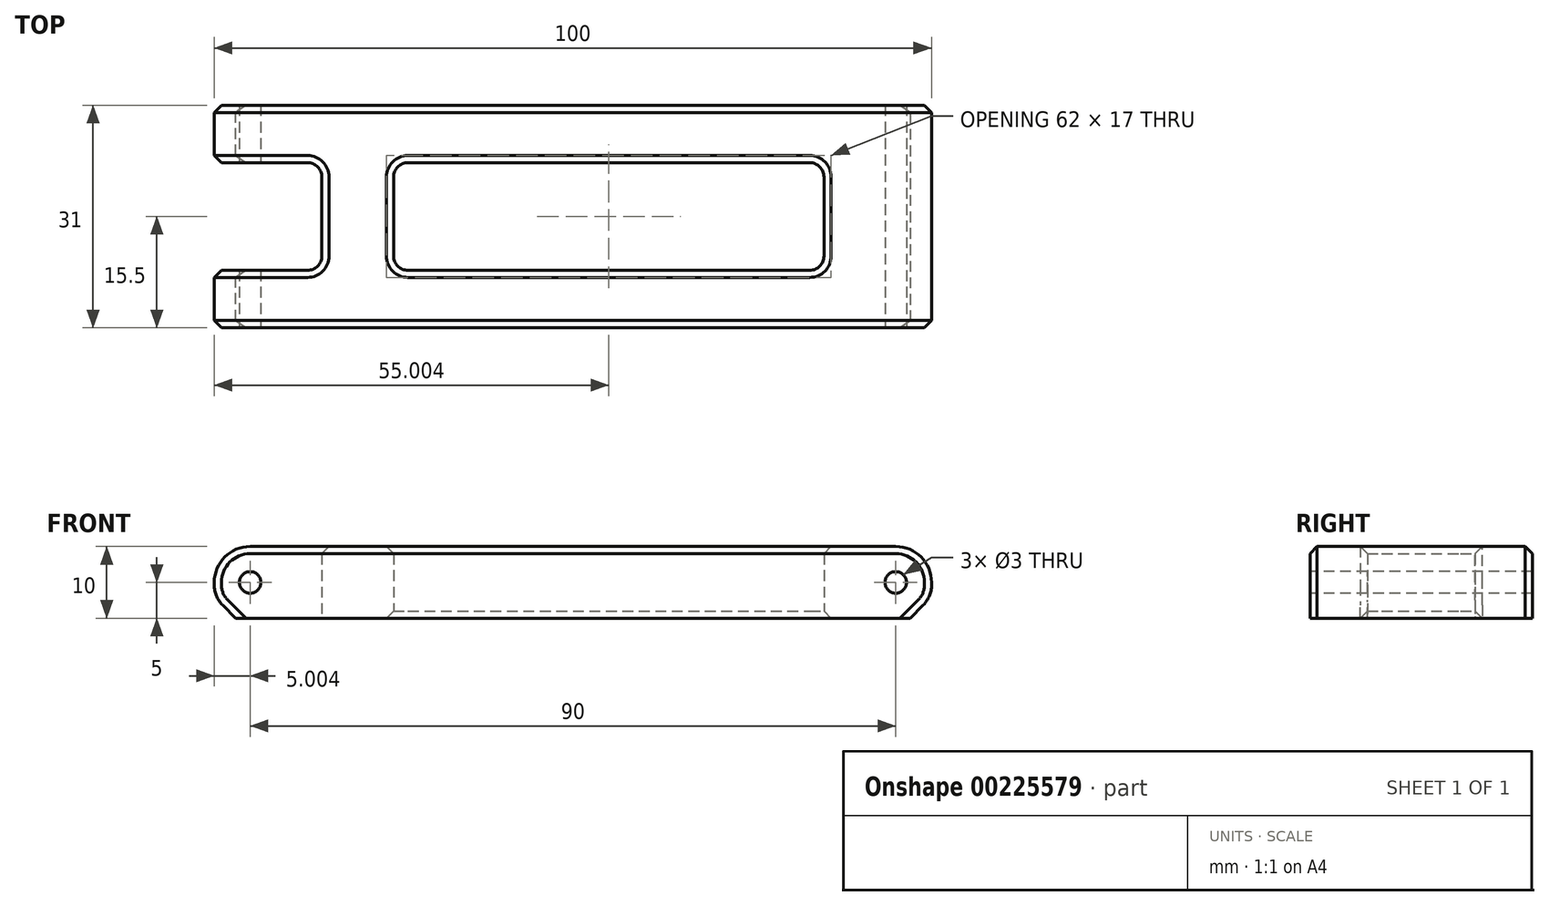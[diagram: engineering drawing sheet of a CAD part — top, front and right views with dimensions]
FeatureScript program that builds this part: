
annotation { "Feature Type Name" : "Feature", "Feature Type Description" : "" }
export const myFeature = defineFeature(function(context is Context, id is Id, definition is map)
    precondition{}
    {
        {
            var Q0;
            Q0=qCreatedBy(makeId("Top.planeOp"),FACE);
            var sketch = newSketch(context, id + "F0", { "sketchPlane" : qUnion([Q0])});
            skLineSegment(sketch, "E0", {"start": v(-23.95, 7.5) * mm, "end": v(-8.95, 7.5) * mm});
            skLineSegment(sketch, "E1", {"start": v(-8.95, 7.5) * mm, "end": v(-8.95, -7.5) * mm});
            skLineSegment(sketch, "E2", {"start": v(-8.95, -7.5) * mm, "end": v(-23.95, -7.5) * mm});
            skLineSegment(sketch, "E3", {"start": v(-23.95, -7.5) * mm, "end": v(-23.95, -15.5) * mm});
            skLineSegment(sketch, "E4", {"start": v(-23.95, -15.5) * mm, "end": v(76.05, -15.5) * mm});
            skLineSegment(sketch, "E5", {"start": v(76.05, -15.5) * mm, "end": v(76.05, 15.5) * mm});
            skLineSegment(sketch, "E6", {"start": v(76.05, 15.5) * mm, "end": v(-23.95, 15.5) * mm});
            skLineSegment(sketch, "E7", {"start": v(-23.95, 15.5) * mm, "end": v(-23.95, 7.5) * mm});
            skLineSegment(sketch, "E8.bottom", {"start": v(1.05, 7.5) * mm, "end": v(61.05, 7.5) * mm});
            skLineSegment(sketch, "E8.top", {"start": v(1.05, -7.5) * mm, "end": v(61.05, -7.5) * mm});
            skLineSegment(sketch, "E8.left", {"start": v(1.05, 7.5) * mm, "end": v(1.05, -7.5) * mm});
            skLineSegment(sketch, "E8.right", {"start": v(61.05, 7.5) * mm, "end": v(61.05, -7.5) * mm});
            skSolve(sketch);
        }
        {
            var Q0;
            Q0=makeQuery(id+"F0.imprint","IMPRINT",FACE,{"disambiguationData":[TD([[makeQuery(id+"F0.imprint","IMPRINT",EDGE,{"derivedFrom":sQuery(id+"F0.wireOp",EDGE,"E0")}),1.0]])]});
            extrude(context, id + "F1", {"entities" : qUnion([Q0]), "depth" : 10 * mm});
        }
        {
            var Q0;
            Q0=makeQuery(id+"F1.opExtrude","CAP_EDGE",EDGE,{"disambiguationData":[OSD([sQuery(id+"F0.wireOp",EDGE,"E7")])],"isStart":false});
            var Q1;
            Q1=makeQuery(id+"F1.opExtrude","CAP_EDGE",EDGE,{"disambiguationData":[OSD([sQuery(id+"F0.wireOp",EDGE,"E3")])],"isStart":false});
            var Q2;
            Q2=makeQuery(id+"F1.opExtrude","CAP_EDGE",EDGE,{"disambiguationData":[OSD([sQuery(id+"F0.wireOp",EDGE,"E5")])],"isStart":false});
            fillet(context, id + "F2", {"entities" : qUnion([Q0, Q1, Q2]), "radius" : 5 * mm, "tangentPropagation" : true, "allowEdgeOverflow" : false});
        }
        {
            var Q0;
            Q0=makeQuery(id+"F1.opExtrude","CAP_EDGE",EDGE,{"disambiguationData":[OSD([sQuery(id+"F0.wireOp",EDGE,"E7")])],"isStart":true});
            var Q1;
            Q1=makeQuery(id+"F1.opExtrude","CAP_EDGE",EDGE,{"disambiguationData":[OSD([sQuery(id+"F0.wireOp",EDGE,"E3")])],"isStart":true});
            var Q2;
            Q2=makeQuery(id+"F1.opExtrude","CAP_EDGE",EDGE,{"disambiguationData":[OSD([sQuery(id+"F0.wireOp",EDGE,"E5")])],"isStart":true});
            chamfer(context, id + "F3", {"entities" : qUnion([Q0, Q1, Q2]), "width" : 3 * mm, "tangentPropagation" : true});
        }
        {
            var Q0;
            {var subQ0=sQuery(id+"F0.wireOp",EDGE,"E5");Q0=makeQuery(id+"F3.opChamfer","BLEND_EDGE",EDGE,{"blendedFrom":[makeQuery(id+"F1.opExtrude","CAP_EDGE",EDGE,{"disambiguationData":[OSD([subQ0])],"isStart":true}),makeQuery(id+"F1.opExtrude","SWEPT_FACE",FACE,{"disambiguationData":[OSD([subQ0])]})],"blendedInto":[makeQuery(id+"F1.opExtrude","SWEPT_FACE",FACE,{"disambiguationData":[OSD([subQ0])]})]});}
            var Q1;
            {var subQ0=sQuery(id+"F0.wireOp",EDGE,"E3");Q1=makeQuery(id+"F3.opChamfer","BLEND_EDGE",EDGE,{"blendedFrom":[makeQuery(id+"F1.opExtrude","CAP_EDGE",EDGE,{"disambiguationData":[OSD([subQ0])],"isStart":true}),makeQuery(id+"F1.opExtrude","SWEPT_FACE",FACE,{"disambiguationData":[OSD([subQ0])]})],"blendedInto":[makeQuery(id+"F1.opExtrude","SWEPT_FACE",FACE,{"disambiguationData":[OSD([subQ0])]})]});}
            var Q2;
            {var subQ0=sQuery(id+"F0.wireOp",EDGE,"E7");Q2=makeQuery(id+"F3.opChamfer","BLEND_EDGE",EDGE,{"blendedFrom":[makeQuery(id+"F1.opExtrude","CAP_EDGE",EDGE,{"disambiguationData":[OSD([subQ0])],"isStart":true}),makeQuery(id+"F1.opExtrude","SWEPT_FACE",FACE,{"disambiguationData":[OSD([subQ0])]})],"blendedInto":[makeQuery(id+"F1.opExtrude","SWEPT_FACE",FACE,{"disambiguationData":[OSD([subQ0])]})]});}
            fillet(context, id + "F4", {"entities" : qUnion([Q0, Q1, Q2]), "radius" : 4 * mm, "tangentPropagation" : true, "allowEdgeOverflow" : false});
        }
        {
            var Q0;
            Q0=makeQuery(id+"F1.opExtrude","SWEPT_EDGE",EDGE,{"disambiguationData":[OSD([sQuery(id+"F0.wireOp",EDGE,"E0"),sQuery(id+"F0.wireOp",EDGE,"E1")])]});
            var Q1;
            Q1=makeQuery(id+"F1.opExtrude","SWEPT_EDGE",EDGE,{"disambiguationData":[OSD([sQuery(id+"F0.wireOp",EDGE,"E1"),sQuery(id+"F0.wireOp",EDGE,"E2")])]});
            var Q2;
            Q2=makeQuery(id+"F1.opExtrude","SWEPT_EDGE",EDGE,{"disambiguationData":[OSD([sQuery(id+"F0.wireOp",EDGE,"E8.bottom"),sQuery(id+"F0.wireOp",EDGE,"E8.left")])]});
            var Q3;
            Q3=makeQuery(id+"F1.opExtrude","SWEPT_EDGE",EDGE,{"disambiguationData":[OSD([sQuery(id+"F0.wireOp",EDGE,"E8.top"),sQuery(id+"F0.wireOp",EDGE,"E8.left")])]});
            var Q4;
            Q4=makeQuery(id+"F1.opExtrude","SWEPT_EDGE",EDGE,{"disambiguationData":[OSD([sQuery(id+"F0.wireOp",EDGE,"E8.bottom"),sQuery(id+"F0.wireOp",EDGE,"E8.right")])]});
            var Q5;
            Q5=makeQuery(id+"F1.opExtrude","SWEPT_EDGE",EDGE,{"disambiguationData":[OSD([sQuery(id+"F0.wireOp",EDGE,"E8.top"),sQuery(id+"F0.wireOp",EDGE,"E8.right")])]});
            fillet(context, id + "F5", {"entities" : qUnion([Q0, Q1, Q2, Q3, Q4, Q5]), "radius" : 2 * mm, "tangentPropagation" : true, "allowEdgeOverflow" : false});
        }
        {
            var Q0;
            Q0=makeQuery(id+"F1.opExtrude","SWEPT_FACE",FACE,{"disambiguationData":[OSD([sQuery(id+"F0.wireOp",EDGE,"E4")])]});
            var sketch = newSketch(context, id + "F6", { "sketchPlane" : qUnion([Q0])});
            skCircle(sketch, "E9", {"center": v(-18.95, 5) * mm, "radius": 1.5 * mm});
            skCircle(sketch, "E10", {"center": v(71.05, 5) * mm, "radius": 1.5 * mm});
            skSolve(sketch);
        }
        {
            var Q0;
            Q0=makeQuery(id+"F6.imprint","IMPRINT",FACE,{"disambiguationData":[TD([[makeQuery(id+"F6.imprint","IMPRINT",EDGE,{"derivedFrom":sQuery(id+"F6.wireOp",EDGE,"E9")}),1.0]])]});
            var Q1;
            Q1=makeQuery(id+"F6.imprint","IMPRINT",FACE,{"disambiguationData":[TD([[makeQuery(id+"F6.imprint","IMPRINT",EDGE,{"derivedFrom":sQuery(id+"F6.wireOp",EDGE,"E10")}),1.0]])]});
            extrude(context, id + "F7", {"entities" : qUnion([Q0, Q1]), "operationType" : NewBodyOperationType.REMOVE, "endBound" : BoundingType.THROUGH_ALL, "oppositeDirection" : true, "depth" : 25 * mm});
        }
        {
            var Q0;
            Q0=makeQuery(id+"F1.opExtrude","CAP_EDGE",EDGE,{"disambiguationData":[OSD([sQuery(id+"F0.wireOp",EDGE,"E0")])],"isStart":false});
            var Q1;
            Q1=makeQuery(id+"F1.opExtrude","CAP_EDGE",EDGE,{"disambiguationData":[OSD([sQuery(id+"F0.wireOp",EDGE,"E6")])],"isStart":false});
            var Q2;
            Q2=makeQuery(id+"F1.opExtrude","CAP_EDGE",EDGE,{"disambiguationData":[OSD([sQuery(id+"F0.wireOp",EDGE,"E8.bottom")])],"isStart":false});
            var Q3;
            Q3=makeQuery(id+"F1.opExtrude","CAP_EDGE",EDGE,{"disambiguationData":[OSD([sQuery(id+"F0.wireOp",EDGE,"E8.bottom")])],"isStart":true});
            var Q4;
            Q4=makeQuery(id+"F1.opExtrude","CAP_EDGE",EDGE,{"disambiguationData":[OSD([sQuery(id+"F0.wireOp",EDGE,"E4")])],"isStart":false});
            chamfer(context, id + "F8", {"entities" : qUnion([Q0, Q1, Q2, Q3, Q4]), "width" : 1 * mm, "tangentPropagation" : true});
        }
    });
